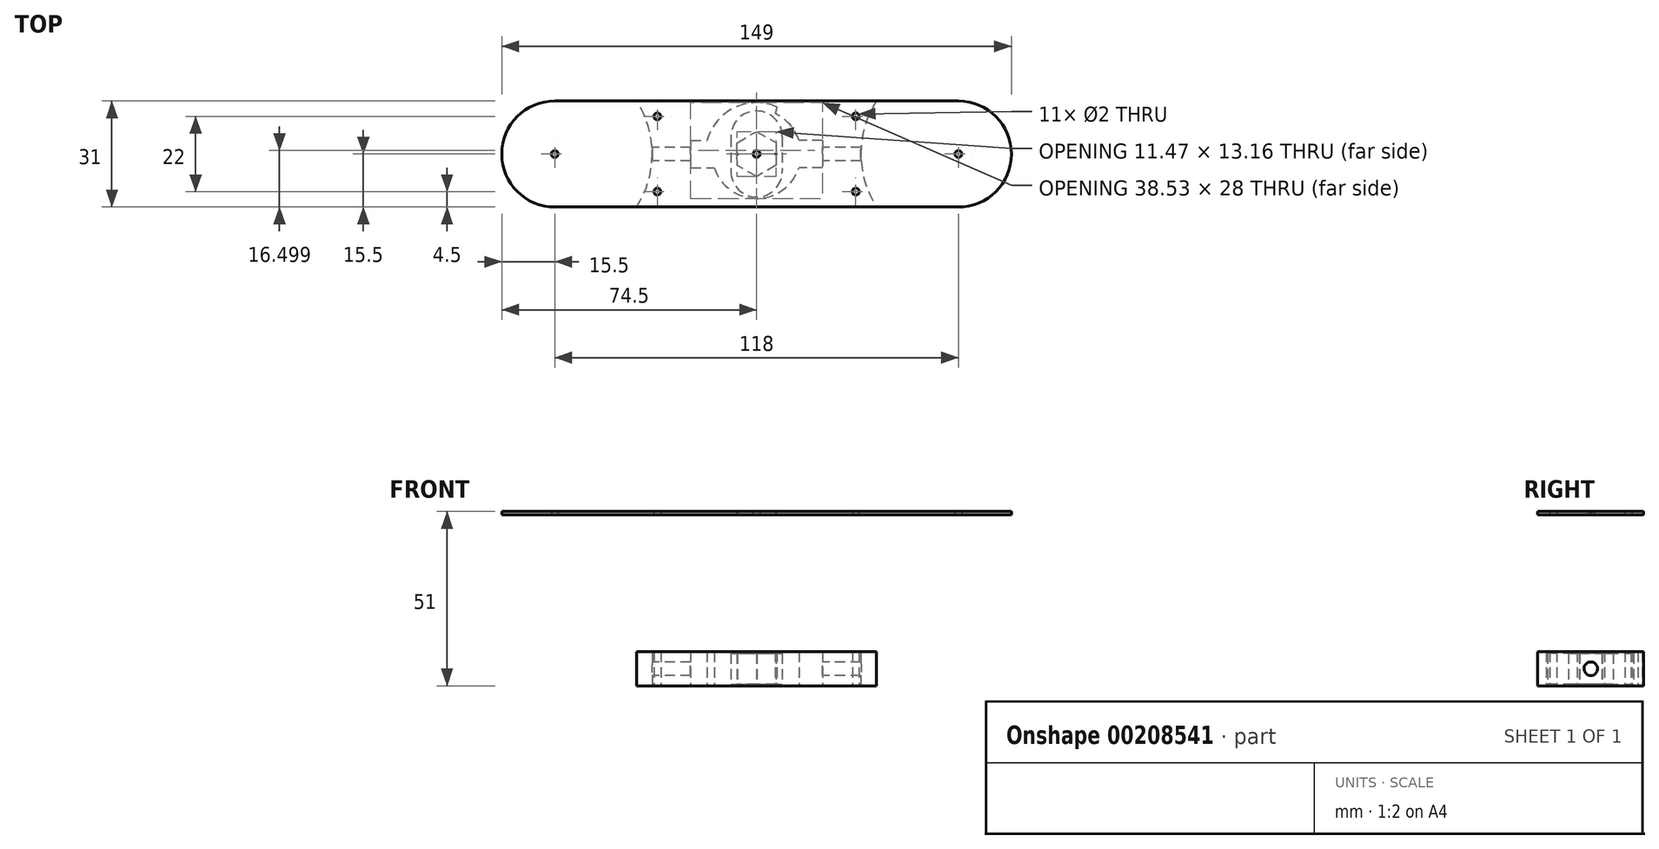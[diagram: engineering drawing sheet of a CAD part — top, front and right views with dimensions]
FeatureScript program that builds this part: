
annotation { "Feature Type Name" : "Feature", "Feature Type Description" : "" }
export const myFeature = defineFeature(function(context is Context, id is Id, definition is map)
    precondition{}
    {
        {
            var Q0;
            Q0=qCreatedBy(makeId("Top.planeOp"),FACE);
            var sketch = newSketch(context, id + "F0", { "sketchPlane" : qUnion([Q0])});
            skCircle(sketch, "E0", {"center": v(59, 0) * mm, "radius": 27.5 * mm});
            skLineSegment(sketch, "E1", {"start": v(26.27, 17) * mm, "end": v(91.54, 17) * mm});
            skCircle(sketch, "E2", {"center": v(-59, 0) * mm, "radius": 27.5 * mm});
            skLineSegment(sketch, "E3", {"start": v(-30.2, -17) * mm, "end": v(-105.64, -17) * mm});
            skCircle(sketch, "E4.0", {"center": v(59, 0) * mm, "radius": 28.5 * mm});
            skCircle(sketch, "E5.0", {"center": v(-59, 0) * mm, "radius": 28.5 * mm});
            skCircle(sketch, "E6", {"center": v(0, 0) * mm, "radius": 13 * mm});
            skCircle(sketch, "E7", {"center": v(59, 0) * mm, "radius": 15.5 * mm});
            skCircle(sketch, "E8", {"center": v(-59, 0) * mm, "radius": 15.5 * mm});
            skLineSegment(sketch, "E9", {"start": v(59.04, 15.5) * mm, "end": v(-59, 15.5) * mm});
            skLineSegment(sketch, "E10", {"start": v(-59.05, -15.5) * mm, "end": v(59, -15.5) * mm});
            skCircle(sketch, "E11", {"center": v(29, 11) * mm, "radius": 1 * mm});
            skCircle(sketch, "E12.MirrorC", {"center": v(-29, 11) * mm, "radius": 1 * mm});
            skCircle(sketch, "E13.MirrorC", {"center": v(29, -11) * mm, "radius": 1 * mm});
            skCircle(sketch, "E14.MirrorC", {"center": v(-29, -11) * mm, "radius": 1 * mm});
            skLineSegment(sketch, "E15.bottom", {"start": v(19.26, 4) * mm, "end": v(9.26, 4) * mm});
            skLineSegment(sketch, "E15.top", {"start": v(19.26, -4) * mm, "end": v(9.26, -4) * mm});
            skLineSegment(sketch, "E15.left", {"start": v(19.26, 4) * mm, "end": v(19.26, -4) * mm});
            skLineSegment(sketch, "E15.right", {"start": v(9.26, 4) * mm, "end": v(9.26, -4) * mm});
            skLineSegment(sketch, "E16.MirrorCS", {"start": v(-19.26, 4) * mm, "end": v(-19.26, -4) * mm});
            skLineSegment(sketch, "E17.MirrorCS", {"start": v(-19.26, 4) * mm, "end": v(-9.26, 4) * mm});
            skLineSegment(sketch, "E18.MirrorCS", {"start": v(-9.26, 4) * mm, "end": v(-9.26, -4) * mm});
            skLineSegment(sketch, "E19.MirrorCS", {"start": v(-19.26, -4) * mm, "end": v(-9.26, -4) * mm});
            skCircle(sketch, "E20", {"center": v(0, 5.08) * mm, "radius": 7.5 * mm});
            skCircle(sketch, "E21.MirrorC", {"center": v(0, -5.08) * mm, "radius": 7.5 * mm});
            skLineSegment(sketch, "E22", {"start": v(7.5, 5.08) * mm, "end": v(7.5, -5.08) * mm});
            skLineSegment(sketch, "E23.MirrorCS", {"start": v(-7.5, 5.08) * mm, "end": v(-7.5, -5.08) * mm});
            skCircle(sketch, "E24.0", {"center": v(0, 0) * mm, "radius": 15 * mm});
            skLineSegment(sketch, "E25", {"start": v(5.95, 13.77) * mm, "end": v(5.43, 11.81) * mm});
            skCircle(sketch, "E26.cCircle", {"center": v(0, 0) * mm, "radius": 5.7 * mm, "construction": true});
            skLineSegment(sketch, "E26.0", {"start": v(-0.07, 6.58) * mm, "end": v(5.66, 3.35) * mm});
            skLineSegment(sketch, "E26.1", {"start": v(5.66, 3.35) * mm, "end": v(5.74, -3.23) * mm});
            skLineSegment(sketch, "E26.2", {"start": v(5.74, -3.23) * mm, "end": v(0.07, -6.58) * mm});
            skLineSegment(sketch, "E26.3", {"start": v(0.07, -6.58) * mm, "end": v(-5.66, -3.35) * mm});
            skLineSegment(sketch, "E26.4", {"start": v(-5.66, -3.35) * mm, "end": v(-5.74, 3.23) * mm});
            skLineSegment(sketch, "E26.5", {"start": v(-5.74, 3.23) * mm, "end": v(-0.07, 6.58) * mm});
            skPoint(sketch, "E26.0.midPoint", {"position": v(2.8, 4.97) * mm});
            skCircle(sketch, "E27", {"center": v(-59, 0) * mm, "radius": 1 * mm});
            skCircle(sketch, "E28", {"center": v(59, 0) * mm, "radius": 1 * mm});
            skCircle(sketch, "E29", {"center": v(0, 0) * mm, "radius": 1 * mm});
            skSolve(sketch);
        }
        {
            var Q0;
            Q0=makeQuery(id+"F0.imprint","IMPRINT",FACE,{"disambiguationData":[TD([[makeQuery(id+"F0.imprint","IMPRINT",EDGE,{"derivedFrom":sQuery(id+"F0.wireOp",EDGE,"E11")}),-1.0]])]});
            var Q1;
            {var subQ0=sQuery(id+"F0.wireOp",EDGE,"E25");Q1=makeQuery(id+"F0.imprint","IMPRINT",FACE,{"disambiguationData":[TD([[makeQuery(id+"F0.imprint","IMPRINT",EDGE,{"derivedFrom":subQ0}),1.0]])]});}
            var Q2;
            {var subQ0=sQuery(id+"F0.wireOp",EDGE,"E19.MirrorCS");var subQ1=sQuery(id+"F0.wireOp",EDGE,"E6");var subQ2=makeQuery(id+"F0.imprint","INTERSECT",VERTEX,{"derivedFrom":[subQ1,subQ0]});Q2=makeQuery(id+"F0.imprint","IMPRINT",FACE,{"disambiguationData":[TD([[makeQuery(id+"F0.imprint","IMPRINT",EDGE,{"disambiguationData":[TD([[subQ2,-1.0]])],"derivedFrom":subQ1}),-1.0]])]});}
            extrude(context, id + "F1", {"entities" : qUnion([Q0, Q1, Q2]), "depth" : 10 * mm, "symmetric" : true});
        }
        {
            var Q0;
            Q0=qCreatedBy(makeId("Right.planeOp"),FACE);
            var sketch = newSketch(context, id + "F2", { "sketchPlane" : qUnion([Q0])});
            skCircle(sketch, "E30", {"center": v(0, 0) * mm, "radius": 2 * mm});
            skSolve(sketch);
        }
        {
            var Q0;
            Q0=makeQuery(id+"F2.imprint","IMPRINT",FACE,{"disambiguationData":[TD([[makeQuery(id+"F2.imprint","IMPRINT",EDGE,{"derivedFrom":sQuery(id+"F2.wireOp",EDGE,"E30")}),1.0]])]});
            extrude(context, id + "F3", {"entities" : qUnion([Q0]), "operationType" : NewBodyOperationType.REMOVE, "depth" : 200 * mm, "symmetric" : true});
        }
        {
            var Q0;
            {var subQ0=sQuery(id+"F0.wireOp",EDGE,"E26.2");Q0=makeQuery(id+"F0.imprint","IMPRINT",FACE,{"disambiguationData":[TD([[makeQuery(id+"F0.imprint","IMPRINT",EDGE,{"derivedFrom":subQ0}),1.0]])]});}
            var Q1;
            {var subQ0=sQuery(id+"F0.wireOp",EDGE,"E22");Q1=makeQuery(id+"F0.imprint","IMPRINT",FACE,{"disambiguationData":[TD([[makeQuery(id+"F0.imprint","IMPRINT",EDGE,{"derivedFrom":subQ0}),-1.0]])]});}
            var Q2;
            {var subQ4=sQuery(id+"F0.wireOp",EDGE,"E26.0");Q2=makeQuery(id+"F0.imprint","IMPRINT",FACE,{"disambiguationData":[TD([[makeQuery(id+"F0.imprint","IMPRINT",EDGE,{"derivedFrom":subQ4}),1.0]])]});}
            var Q3;
            {var subQ0=sQuery(id+"F0.wireOp",EDGE,"E23.MirrorCS");Q3=makeQuery(id+"F0.imprint","IMPRINT",FACE,{"disambiguationData":[TD([[makeQuery(id+"F0.imprint","IMPRINT",EDGE,{"derivedFrom":subQ0}),1.0]])]});}
            extrude(context, id + "F4", {"entities" : qUnion([Q0, Q1, Q2, Q3]), "depth" : 9 * mm, "symmetric" : true});
        }
        {
            var Q0;
            Q0=makeQuery(id+"F0.imprint","IMPRINT",FACE,{"disambiguationData":[TD([[makeQuery(id+"F0.imprint","IMPRINT",EDGE,{"derivedFrom":sQuery(id+"F0.wireOp",EDGE,"E27")}),-1.0]])]});
            var Q1;
            {var subQ0=sQuery(id+"F0.wireOp",EDGE,"E9");var subQ1=sQuery(id+"F0.wireOp",EDGE,"E2");var subQ2=makeQuery(id+"F0.imprint","INTERSECT",VERTEX,{"derivedFrom":[subQ1,subQ0]});Q1=makeQuery(id+"F0.imprint","IMPRINT",FACE,{"disambiguationData":[TD([[makeQuery(id+"F0.imprint","IMPRINT",EDGE,{"disambiguationData":[TD([[subQ2,1.0]])],"derivedFrom":subQ1}),1.0]])]});}
            var Q2;
            {var subQ0=sQuery(id+"F0.wireOp",EDGE,"E9");var subQ1=sQuery(id+"F0.wireOp",EDGE,"E2");var subQ2=makeQuery(id+"F0.imprint","INTERSECT",VERTEX,{"derivedFrom":[subQ1,subQ0]});Q2=makeQuery(id+"F0.imprint","IMPRINT",FACE,{"disambiguationData":[TD([[makeQuery(id+"F0.imprint","IMPRINT",EDGE,{"disambiguationData":[TD([[subQ2,1.0]])],"derivedFrom":subQ1}),-1.0]])]});}
            var Q3;
            Q3=makeQuery(id+"F0.imprint","IMPRINT",FACE,{"disambiguationData":[TD([[makeQuery(id+"F0.imprint","IMPRINT",EDGE,{"derivedFrom":sQuery(id+"F0.wireOp",EDGE,"E11")}),-1.0]])]});
            var Q4;
            {var subQ0=sQuery(id+"F0.wireOp",EDGE,"E9");var subQ1=sQuery(id+"F0.wireOp",EDGE,"E0");var subQ2=makeQuery(id+"F0.imprint","INTERSECT",VERTEX,{"derivedFrom":[subQ1,subQ0]});Q4=makeQuery(id+"F0.imprint","IMPRINT",FACE,{"disambiguationData":[TD([[makeQuery(id+"F0.imprint","IMPRINT",EDGE,{"disambiguationData":[TD([[subQ2,-1.0]])],"derivedFrom":subQ1}),1.0]])]});}
            var Q5;
            Q5=makeQuery(id+"F0.imprint","IMPRINT",FACE,{"disambiguationData":[TD([[makeQuery(id+"F0.imprint","IMPRINT",EDGE,{"derivedFrom":sQuery(id+"F0.wireOp",EDGE,"E28")}),-1.0]])]});
            var Q6;
            {var subQ0=sQuery(id+"F0.wireOp",EDGE,"E15.left");Q6=makeQuery(id+"F0.imprint","IMPRINT",FACE,{"disambiguationData":[TD([[makeQuery(id+"F0.imprint","IMPRINT",EDGE,{"derivedFrom":subQ0}),-1.0]])]});}
            var Q7;
            {var subQ0=sQuery(id+"F0.wireOp",EDGE,"E15.bottom");var subQ1=sQuery(id+"F0.wireOp",EDGE,"E6");var subQ2=makeQuery(id+"F0.imprint","INTERSECT",VERTEX,{"derivedFrom":[subQ1,subQ0]});Q7=makeQuery(id+"F0.imprint","IMPRINT",FACE,{"disambiguationData":[TD([[makeQuery(id+"F0.imprint","IMPRINT",EDGE,{"disambiguationData":[TD([[subQ2,1.0]])],"derivedFrom":subQ1}),-1.0]])]});}
            var Q8;
            {var subQ0=sQuery(id+"F0.wireOp",EDGE,"E25");Q8=makeQuery(id+"F0.imprint","IMPRINT",FACE,{"disambiguationData":[TD([[makeQuery(id+"F0.imprint","IMPRINT",EDGE,{"derivedFrom":subQ0}),1.0]])]});}
            var Q9;
            {var subQ0=sQuery(id+"F0.wireOp",EDGE,"E19.MirrorCS");var subQ1=sQuery(id+"F0.wireOp",EDGE,"E6");var subQ2=makeQuery(id+"F0.imprint","INTERSECT",VERTEX,{"derivedFrom":[subQ1,subQ0]});Q9=makeQuery(id+"F0.imprint","IMPRINT",FACE,{"disambiguationData":[TD([[makeQuery(id+"F0.imprint","IMPRINT",EDGE,{"disambiguationData":[TD([[subQ2,-1.0]])],"derivedFrom":subQ1}),-1.0]])]});}
            var Q10;
            {var subQ0=sQuery(id+"F0.wireOp",EDGE,"E16.MirrorCS");Q10=makeQuery(id+"F0.imprint","IMPRINT",FACE,{"disambiguationData":[TD([[makeQuery(id+"F0.imprint","IMPRINT",EDGE,{"derivedFrom":subQ0}),1.0]])]});}
            var Q11;
            {var subQ0=sQuery(id+"F0.wireOp",EDGE,"E17.MirrorCS");var subQ1=sQuery(id+"F0.wireOp",EDGE,"E6");var subQ2=makeQuery(id+"F0.imprint","INTERSECT",VERTEX,{"derivedFrom":[subQ1,subQ0]});Q11=makeQuery(id+"F0.imprint","IMPRINT",FACE,{"disambiguationData":[TD([[makeQuery(id+"F0.imprint","IMPRINT",EDGE,{"disambiguationData":[TD([[subQ2,-1.0]])],"derivedFrom":subQ1}),-1.0]])]});}
            var Q12;
            {var subQ0=sQuery(id+"F0.wireOp",EDGE,"E25");Q12=makeQuery(id+"F0.imprint","IMPRINT",FACE,{"disambiguationData":[TD([[makeQuery(id+"F0.imprint","IMPRINT",EDGE,{"derivedFrom":subQ0}),-1.0]])]});}
            var Q13;
            {var subQ4=sQuery(id+"F0.wireOp",EDGE,"E15.right");Q13=makeQuery(id+"F0.imprint","IMPRINT",FACE,{"disambiguationData":[TD([[makeQuery(id+"F0.imprint","IMPRINT",EDGE,{"derivedFrom":subQ4}),-1.0]])]});}
            var Q14;
            {var subQ5=sQuery(id+"F0.wireOp",EDGE,"E15.right");Q14=makeQuery(id+"F0.imprint","IMPRINT",FACE,{"disambiguationData":[TD([[makeQuery(id+"F0.imprint","IMPRINT",EDGE,{"derivedFrom":subQ5}),1.0]])]});}
            var Q15;
            {var subQ5=sQuery(id+"F0.wireOp",EDGE,"E18.MirrorCS");Q15=makeQuery(id+"F0.imprint","IMPRINT",FACE,{"disambiguationData":[TD([[makeQuery(id+"F0.imprint","IMPRINT",EDGE,{"derivedFrom":subQ5}),-1.0]])]});}
            var Q16;
            {var subQ4=sQuery(id+"F0.wireOp",EDGE,"E26.0");Q16=makeQuery(id+"F0.imprint","IMPRINT",FACE,{"disambiguationData":[TD([[makeQuery(id+"F0.imprint","IMPRINT",EDGE,{"derivedFrom":subQ4}),1.0]])]});}
            var Q17;
            {var subQ0=sQuery(id+"F0.wireOp",EDGE,"E26.2");Q17=makeQuery(id+"F0.imprint","IMPRINT",FACE,{"disambiguationData":[TD([[makeQuery(id+"F0.imprint","IMPRINT",EDGE,{"derivedFrom":subQ0}),1.0]])]});}
            var Q18;
            {var subQ0=sQuery(id+"F0.wireOp",EDGE,"E22");Q18=makeQuery(id+"F0.imprint","IMPRINT",FACE,{"disambiguationData":[TD([[makeQuery(id+"F0.imprint","IMPRINT",EDGE,{"derivedFrom":subQ0}),-1.0]])]});}
            var Q19;
            {var subQ0=sQuery(id+"F0.wireOp",EDGE,"E23.MirrorCS");Q19=makeQuery(id+"F0.imprint","IMPRINT",FACE,{"disambiguationData":[TD([[makeQuery(id+"F0.imprint","IMPRINT",EDGE,{"derivedFrom":subQ0}),1.0]])]});}
            var Q20;
            {var subQ5=sQuery(id+"F0.wireOp",EDGE,"E26.2");Q20=makeQuery(id+"F0.imprint","IMPRINT",FACE,{"disambiguationData":[TD([[makeQuery(id+"F0.imprint","IMPRINT",EDGE,{"derivedFrom":subQ5}),-1.0]])]});}
            var Q21;
            Q21=makeQuery(id+"F0.imprint","IMPRINT",FACE,{"disambiguationData":[TD([[makeQuery(id+"F0.imprint","IMPRINT",EDGE,{"derivedFrom":sQuery(id+"F0.wireOp",EDGE,"E29")}),-1.0]])]});
            var Q22;
            {var subQ0=sQuery(id+"F0.wireOp",EDGE,"E26.0");Q22=makeQuery(id+"F0.imprint","IMPRINT",FACE,{"disambiguationData":[TD([[makeQuery(id+"F0.imprint","IMPRINT",EDGE,{"derivedFrom":subQ0}),-1.0]])]});}
            var Q23;
            {var subQ0=sQuery(id+"F0.wireOp",EDGE,"E9");var subQ1=sQuery(id+"F0.wireOp",EDGE,"E0");var subQ2=makeQuery(id+"F0.imprint","INTERSECT",VERTEX,{"derivedFrom":[subQ1,subQ0]});Q23=makeQuery(id+"F0.imprint","IMPRINT",FACE,{"disambiguationData":[TD([[makeQuery(id+"F0.imprint","IMPRINT",EDGE,{"disambiguationData":[TD([[subQ2,-1.0]])],"derivedFrom":subQ1}),-1.0]])]});}
            extrude(context, id + "F5", {"entities" : qUnion([Q0, Q1, Q2, Q3, Q4, Q5, Q6, Q7, Q8, Q9, Q10, Q11, Q12, Q13, Q14, Q15, Q16, Q17, Q18, Q19, Q20, Q21, Q22, Q23]), "depth" : 46 * mm, "hasSecondDirection" : true, "secondDirectionOppositeDirection" : false, "secondDirectionDepth" : 45 * mm});
        }
    });
